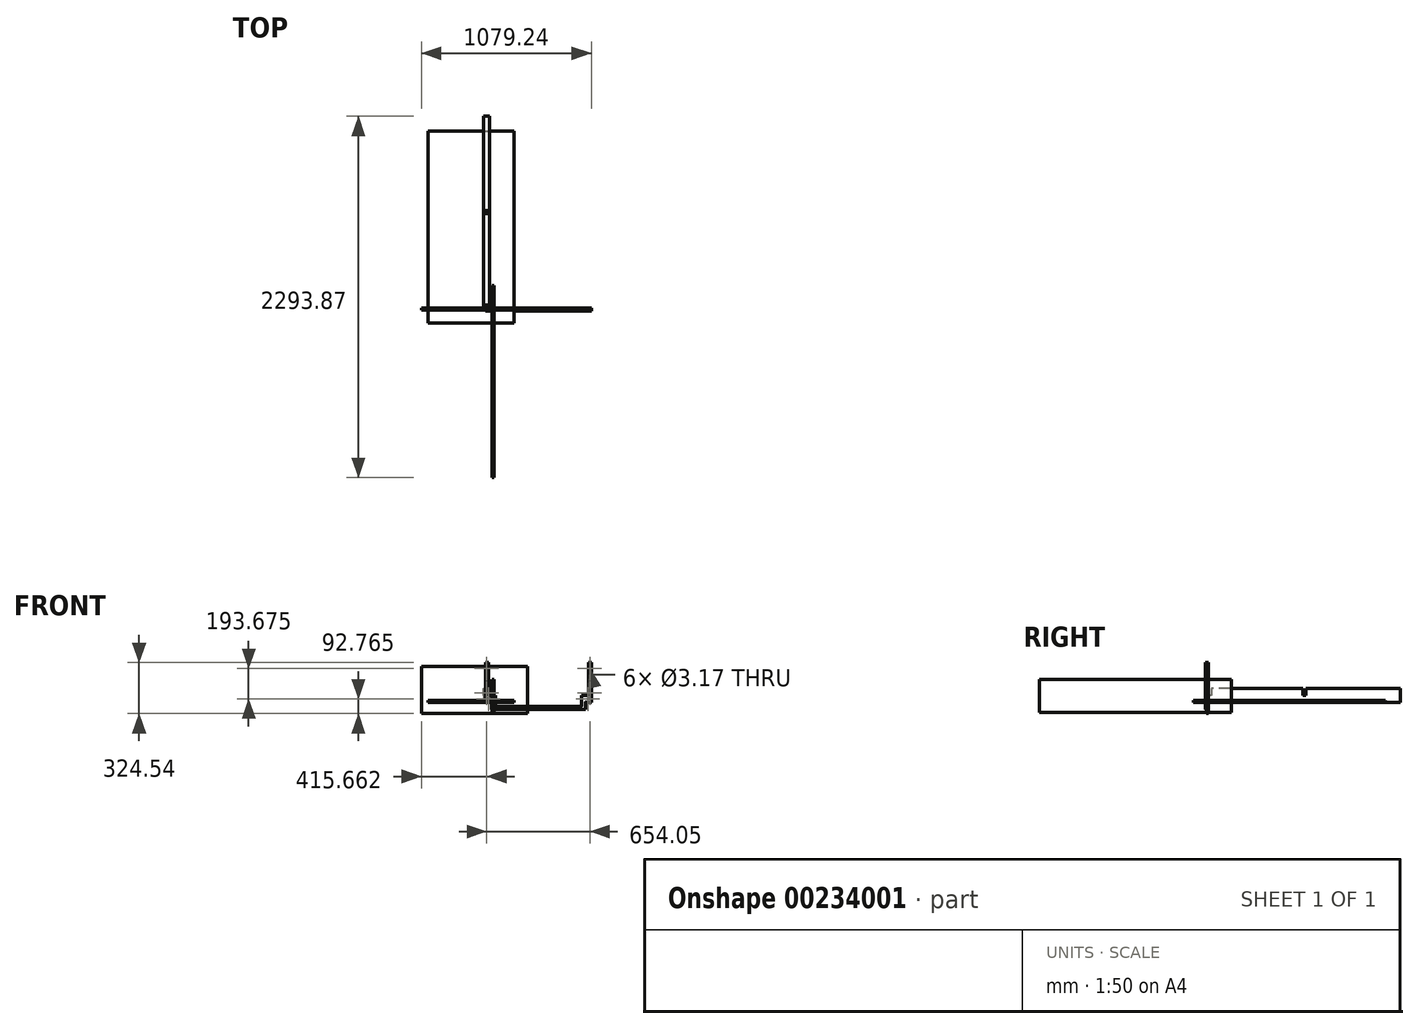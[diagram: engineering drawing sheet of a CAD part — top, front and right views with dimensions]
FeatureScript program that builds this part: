
annotation { "Feature Type Name" : "Feature", "Feature Type Description" : "" }
export const myFeature = defineFeature(function(context is Context, id is Id, definition is map)
    precondition{}
    {
        {
            var Q0;
            Q0=qCreatedBy(makeId("Front.planeOp"),FACE);
            var sketch = newSketch(context, id + "F0", { "sketchPlane" : qUnion([Q0])});
            skLineSegment(sketch, "E0.bottom", {"start": v(-24.4, 44.45) * mm, "end": v(-5.34, 44.45) * mm});
            skLineSegment(sketch, "E0.left", {"start": v(-43.44, 44.45) * mm, "end": v(-43.44, 0) * mm});
            skLineSegment(sketch, "E1", {"start": v(-43.44, 0) * mm, "end": v(-11.7, 0) * mm});
            skLineSegment(sketch, "E2", {"start": v(20.06, -25.4) * mm, "end": v(293.1, -25.4) * mm});
            skLineSegment(sketch, "E3", {"start": v(-43.44, 254) * mm, "end": v(-43.44, 0) * mm});
            skLineSegment(sketch, "E4", {"start": v(-43.44, 254) * mm, "end": v(-24.4, 254) * mm});
            skLineSegment(sketch, "E5", {"start": v(-24.4, 254) * mm, "end": v(-24.4, 50.8) * mm});
            skLineSegment(sketch, "E6", {"start": v(-5.34, -44.45) * mm, "end": v(293.1, -44.45) * mm});
            skLineSegment(sketch, "E7", {"start": v(-5.34, 44.45) * mm, "end": v(20.06, 44.45) * mm});
            skLineSegment(sketch, "E8", {"start": v(20.06, 44.45) * mm, "end": v(20.06, -19.05) * mm});
            skLineSegment(sketch, "E9", {"start": v(-11.7, 254) * mm, "end": v(-11.7, 44.45) * mm, "construction": true});
            skLineSegment(sketch, "E10", {"start": v(-11.7, 254) * mm, "end": v(597.9, 254) * mm, "construction": true});
            skLineSegment(sketch, "E11", {"start": v(293.1, 254) * mm, "end": v(293.1, -69.8) * mm, "construction": true});
            skPoint(sketch, "E12.orphan", {"position": v(201.58, -25.4) * mm});
            skPoint(sketch, "E13.orphan", {"position": v(201.58, -44.45) * mm});
            skLineSegment(sketch, "E14", {"start": v(-5.34, 0) * mm, "end": v(-5.34, -44.45) * mm});
            skLineSegment(sketch, "E15.MirrorCS", {"start": v(629.66, 254) * mm, "end": v(610.6, 254) * mm});
            skLineSegment(sketch, "E16.MirrorCS", {"start": v(610.6, 44.45) * mm, "end": v(591.56, 44.45) * mm});
            skLineSegment(sketch, "E17.MirrorCS", {"start": v(629.66, 44.45) * mm, "end": v(629.66, 0) * mm});
            skLineSegment(sketch, "E18.MirrorCS", {"start": v(591.56, 44.45) * mm, "end": v(566.16, 44.45) * mm});
            skPoint(sketch, "E19.MirrorP", {"position": v(384.64, -44.45) * mm});
            skLineSegment(sketch, "E20.MirrorCS", {"start": v(566.16, 44.45) * mm, "end": v(566.16, -19.05) * mm});
            skLineSegment(sketch, "E21.MirrorCS", {"start": v(610.6, 254) * mm, "end": v(610.6, 50.8) * mm});
            skPoint(sketch, "E22.MirrorP", {"position": v(384.64, -25.4) * mm});
            skLineSegment(sketch, "E23.MirrorCS", {"start": v(591.56, 0) * mm, "end": v(591.56, -44.45) * mm});
            skLineSegment(sketch, "E24.MirrorCS", {"start": v(629.66, 254) * mm, "end": v(629.66, 0) * mm});
            skLineSegment(sketch, "E25.MirrorCS", {"start": v(591.56, -44.45) * mm, "end": v(293.1, -44.45) * mm});
            skLineSegment(sketch, "E26.MirrorCS", {"start": v(629.66, 0) * mm, "end": v(597.9, 0) * mm});
            skLineSegment(sketch, "E27.MirrorCS", {"start": v(566.16, -25.4) * mm, "end": v(293.1, -25.4) * mm});
            skLineSegment(sketch, "E28", {"start": v(-33.92, 254) * mm, "end": v(-33.92, 215.9) * mm, "construction": true});
            skCircle(sketch, "E29", {"center": v(-33.92, 215.9) * mm, "radius": 1.59 * mm});
            skLineSegment(sketch, "E30", {"start": v(-33.92, 215.9) * mm, "end": v(-33.92, 60.64) * mm, "construction": true});
            skCircle(sketch, "E31", {"center": v(-33.92, 60.64) * mm, "radius": 1.59 * mm});
            skPoint(sketch, "E32.endSnap0", {"position": v(-43.44, 22.23) * mm});
            skCircle(sketch, "E33.MirrorC", {"center": v(620.13, 215.9) * mm, "radius": 1.59 * mm});
            skCircle(sketch, "E34.MirrorC", {"center": v(620.13, 60.64) * mm, "radius": 1.59 * mm});
            skLineSegment(sketch, "E35", {"start": v(-33.92, 60.64) * mm, "end": v(-23.74, 22.23) * mm, "construction": true});
            skCircle(sketch, "E36", {"center": v(-23.74, 22.23) * mm, "radius": 1.59 * mm});
            skCircle(sketch, "E37.MirrorC", {"center": v(609.96, 22.23) * mm, "radius": 1.59 * mm});
            skLineSegment(sketch, "E38.MirrorCS", {"start": v(620.13, 60.64) * mm, "end": v(609.96, 22.23) * mm, "construction": true});
            skArc(sketch, "E39", {"start": v(20.06, -19.05) * mm, "mid": v(16.88, -22.22) * mm, "end": v(20.06, -25.4) * mm});
            skArc(sketch, "E40", {"start": v(-24.4, 50.8) * mm, "mid": v(-27.57, 47.63) * mm, "end": v(-24.4, 44.45) * mm});
            skArc(sketch, "E41", {"start": v(-5.34, 0) * mm, "mid": v(-8.52, 3.17) * mm, "end": v(-11.7, 0) * mm});
            skArc(sketch, "E42.MirrorCS", {"start": v(610.6, 50.8) * mm, "mid": v(613.78, 47.63) * mm, "end": v(610.6, 44.45) * mm});
            skArc(sketch, "E43.MirrorCS", {"start": v(591.56, 0) * mm, "mid": v(594.73, 3.18) * mm, "end": v(597.9, 0) * mm});
            skArc(sketch, "E44.MirrorCS", {"start": v(566.16, -19.05) * mm, "mid": v(569.33, -22.22) * mm, "end": v(566.16, -25.4) * mm});
            skSolve(sketch);
        }
        {
            var Q0;
            Q0=makeQuery(id+"F0.imprint","IMPRINT",FACE,{"disambiguationData":[TD([[makeQuery(id+"F0.imprint","IMPRINT",EDGE,{"derivedFrom":sQuery(id+"F0.wireOp",EDGE,"E0.bottom")}),-1.0]])]});
            extrude(context, id + "F1", {"entities" : qUnion([Q0]), "depth" : 19.05 * mm});
        }
        {
            var Q0;
            Q0=qCreatedBy(makeId("Front.planeOp"),FACE);
            var sketch = newSketch(context, id + "F2", { "sketchPlane" : qUnion([Q0])});
            skLineSegment(sketch, "E45.bottom", {"start": v(-53.15, 88.9) * mm, "end": v(-15.05, 88.9) * mm});
            skLineSegment(sketch, "E45.top", {"start": v(-53.15, 0) * mm, "end": v(-15.05, 0) * mm});
            skLineSegment(sketch, "E45.left", {"start": v(-53.15, 88.9) * mm, "end": v(-53.15, 0) * mm});
            skLineSegment(sketch, "E45.right", {"start": v(-15.05, 88.9) * mm, "end": v(-15.05, 0) * mm});
            skSolve(sketch);
        }
        {
            var Q0;
            Q0 = qSketchRegion(id + "F2", true);
            extrude(context, id + "F3", {"entities" : qUnion([Q0]), "oppositeDirection" : true, "depth" : 1219.2 * mm});
        }
        {
            var Q0;
            Q0=makeQuery(id+"F3.opExtrude","SWEPT_FACE",FACE,{"disambiguationData":[OSD([sQuery(id+"F2.wireOp",EDGE,"E45.right")])]});
            var sketch = newSketch(context, id + "F4", { "sketchPlane" : qUnion([Q0])});
            skLineSegment(sketch, "E46", {"start": v(0, 88.9) * mm, "end": v(19.05, 88.9) * mm});
            skLineSegment(sketch, "E47", {"start": v(19.05, 88.9) * mm, "end": v(19.05, 44.45) * mm});
            skLineSegment(sketch, "E48", {"start": v(19.05, 44.45) * mm, "end": v(0, 44.45) * mm});
            skLineSegment(sketch, "E49", {"start": v(0, 44.45) * mm, "end": v(0, 88.9) * mm});
            skSolve(sketch);
        }
        {
            var Q0;
            Q0 = qSketchRegion(id + "F4", true);
            extrude(context, id + "F5", {"entities" : qUnion([Q0]), "operationType" : NewBodyOperationType.REMOVE, "oppositeDirection" : true, "depth" : 50.8 * mm});
        }
        {
            var Q0;
            Q0=qCreatedBy(makeId("Front.planeOp"),FACE);
            cPlane(context, id + "F6", {"entities" : qUnion([Q0]), "cplaneType" : CPlaneType.OFFSET, "offset" : 609.6 * mm, "oppositeDirection" : true, "width" : 152.4 * mm, "height" : 152.4 * mm});
        }
        {
            var Q0;
            Q0=makeQuery(id+"F3.opExtrude","SWEPT_FACE",FACE,{"disambiguationData":[OSD([sQuery(id+"F2.wireOp",EDGE,"E45.right")])]});
            var sketch = newSketch(context, id + "F7", { "sketchPlane" : qUnion([Q0])});
            skLineSegment(sketch, "E50.right", {"start": v(600.08, 88.9) * mm, "end": v(600.08, 44.45) * mm});
            skLineSegment(sketch, "E51.MirrorCS", {"start": v(619.13, 88.9) * mm, "end": v(619.13, 44.45) * mm});
            skLineSegment(sketch, "E52", {"start": v(600.08, 88.9) * mm, "end": v(619.13, 88.9) * mm});
            skLineSegment(sketch, "E53", {"start": v(600.08, 44.45) * mm, "end": v(619.13, 44.45) * mm});
            skSolve(sketch);
        }
        {
            var Q0;
            Q0=makeQuery(id+"F7.imprint","IMPRINT",FACE,{"disambiguationData":[TD([[makeQuery(id+"F7.imprint","IMPRINT",EDGE,{"derivedFrom":sQuery(id+"F7.wireOp",EDGE,"E50.right")}),1.0]])]});
            extrude(context, id + "F8", {"entities" : qUnion([Q0]), "operationType" : NewBodyOperationType.REMOVE, "oppositeDirection" : true, "depth" : 50.8 * mm});
        }
        {
            var Q0;
            Q0=qCreatedBy(makeId("Front.planeOp"),FACE);
            var sketch = newSketch(context, id + "F9", { "sketchPlane" : qUnion([Q0])});
            skLineSegment(sketch, "E54.bottom", {"start": v(-449.58, 227.9) * mm, "end": v(223.52, 227.9) * mm});
            skLineSegment(sketch, "E54.top", {"start": v(-449.58, -70.54) * mm, "end": v(223.52, -70.54) * mm});
            skLineSegment(sketch, "E54.left", {"start": v(-449.58, 227.9) * mm, "end": v(-449.58, -70.54) * mm});
            skLineSegment(sketch, "E54.right", {"start": v(223.52, 227.9) * mm, "end": v(223.52, -70.54) * mm});
            skSolve(sketch);
        }
        {
            var Q0;
            Q0 = qSketchRegion(id + "F9", true);
            extrude(context, id + "F10", {"entities" : qUnion([Q0]), "depth" : 12.7 * mm});
        }
        {
            var Q0;
            Q0=qCreatedBy(makeId("Right.planeOp"),FACE);
            var sketch = newSketch(context, id + "F11", { "sketchPlane" : qUnion([Q0])});
            skLineSegment(sketch, "E55.bottom", {"start": v(-1074.67, 147.17) * mm, "end": v(144.53, 147.17) * mm});
            skLineSegment(sketch, "E55.top", {"start": v(-1074.67, -62.38) * mm, "end": v(144.53, -62.38) * mm});
            skLineSegment(sketch, "E55.left", {"start": v(-1074.67, 147.17) * mm, "end": v(-1074.67, -62.38) * mm});
            skLineSegment(sketch, "E55.right", {"start": v(144.53, 147.17) * mm, "end": v(144.53, -62.38) * mm});
            skSolve(sketch);
        }
        {
            var Q0;
            Q0=makeQuery(id+"F11.imprint","IMPRINT",FACE,{"disambiguationData":[TD([[makeQuery(id+"F11.imprint","IMPRINT",EDGE,{"derivedFrom":sQuery(id+"F11.wireOp",EDGE,"E55.bottom")}),-1.0]])]});
            extrude(context, id + "F12", {"entities" : qUnion([Q0]), "depth" : 12.7 * mm});
        }
        {
            var Q0;
            Q0=qCreatedBy(makeId("Top.planeOp"),FACE);
            var sketch = newSketch(context, id + "F13", { "sketchPlane" : qUnion([Q0])});
            skLineSegment(sketch, "E56.bottom", {"start": v(-406.5, 1123.74) * mm, "end": v(139.6, 1123.74) * mm});
            skLineSegment(sketch, "E56.top", {"start": v(-406.5, -95.46) * mm, "end": v(139.6, -95.46) * mm});
            skLineSegment(sketch, "E56.left", {"start": v(-406.5, 1123.74) * mm, "end": v(-406.5, -95.46) * mm});
            skLineSegment(sketch, "E56.right", {"start": v(139.6, 1123.74) * mm, "end": v(139.6, -95.46) * mm});
            skSolve(sketch);
        }
        {
            var Q0;
            Q0=makeQuery(id+"F13.imprint","IMPRINT",FACE,{"disambiguationData":[TD([[makeQuery(id+"F13.imprint","IMPRINT",EDGE,{"derivedFrom":sQuery(id+"F13.wireOp",EDGE,"E56.bottom")}),-1.0]])]});
            extrude(context, id + "F14", {"entities" : qUnion([Q0]), "depth" : 12.7 * mm});
        }
    });
